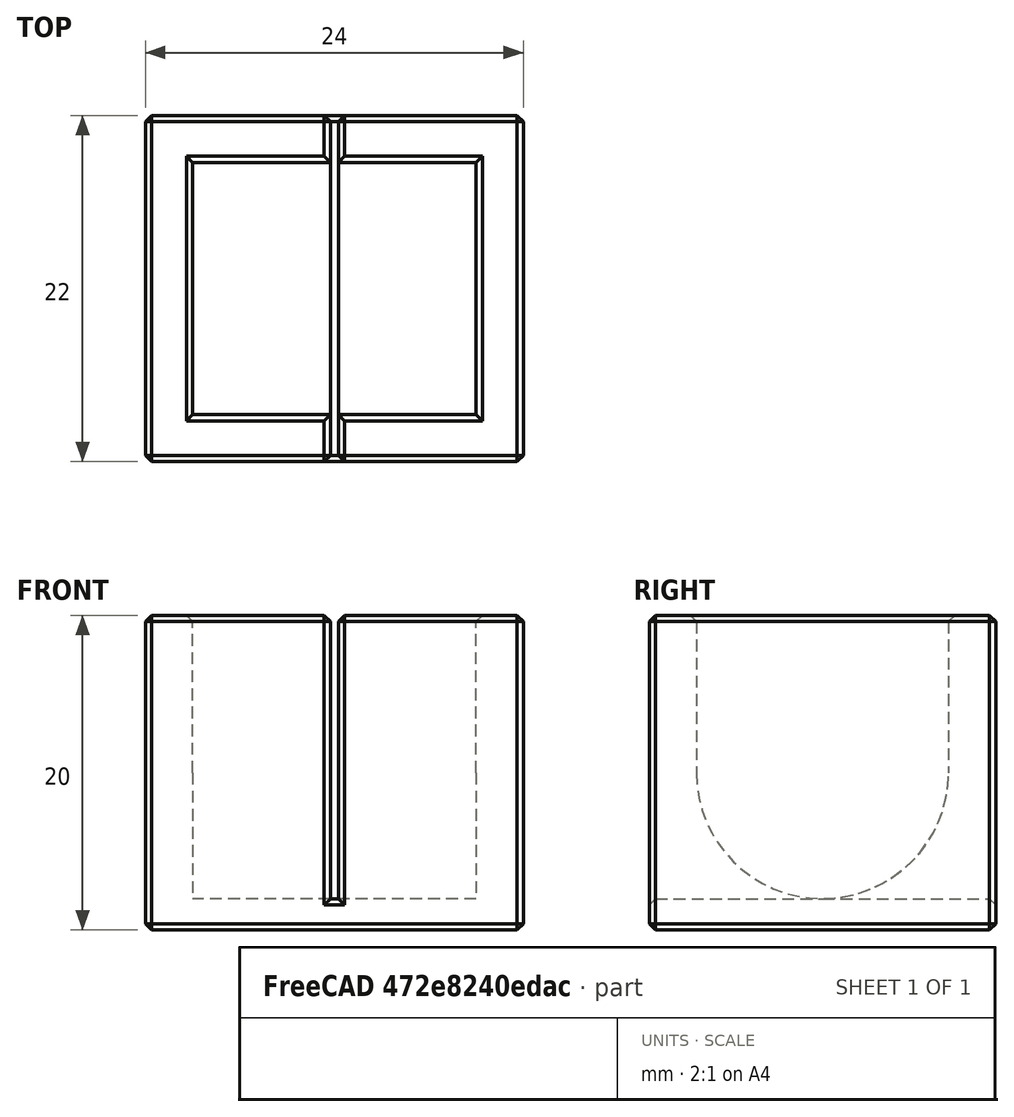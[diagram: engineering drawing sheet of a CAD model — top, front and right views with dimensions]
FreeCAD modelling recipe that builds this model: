
FCSTD DOCUMENT  (FreeCAD 0.19R24291 (Git))
Label: silicon-spacer-cut-template
License: Other
LicenseURL: GPL3
objects: Part::Box×3, Part::Cut×2, Part::Cylinder×1, Part::MultiFuse×1, Part::Chamfer×1
note: 8 computed .brp shape members not serialized (recipe doc carries the construction recipe); baked Part::Feature solids carry a one-line shape summary decoded from their .brp

FEATURE [Part::Cylinder] Cylinder
  Angle = 360
  AttacherType = Attacher::AttachEngine3D
  Height = 18
  Placement = pos=(8,0,10) rot=(0,1,0;4.71239rad)
  Radius = 8
FEATURE [Part::Box] Box  label="Cube"
  AttacherType = Attacher::AttachEngine3D
  Height = 20
  Length = 24
  Placement = pos=(-13,-11,0) rot=(0,0,1;0rad)
  Width = 22
FEATURE [Part::Box] Box001  label="Cube001"
  AttacherType = Attacher::AttachEngine3D
  Height = 10
  Length = 18
  Placement = pos=(-10,-8,10) rot=(0,0,1;0rad)
  Width = 16
FEATURE [Part::MultiFuse] Fusion
  Shapes = -> [Box001,Cylinder]
FEATURE [Part::Cut] Cut
  Base = -> Box
  Tool = -> Fusion
FEATURE [Part::Box] Box002  label="Cube002"
  AttacherType = Attacher::AttachEngine3D
  Height = 24
  Length = 0.5
  Placement = pos=(-1.25,-13,2) rot=(0,0,1;0rad)
  Width = 26
FEATURE [Part::Cut] Cut001
  Base = -> Cut
  Tool = -> Box002
FEATURE [Part::Chamfer] Chamfer
  Base = -> Cut001
  Edges = 30 edges r=0.4: [Edge1,Edge2,Edge3,Edge4,Edge5,Edge6,Edge7,Edge8,Edge9,Edge10,Edge11,Edge12,Edge13,Edge14,Edge15,Edge16,Edge17,Edge18,Edge19,Edge20,Edge21,Edge22,Edge23,Edge24,Edge25,Edge26,Edge27,Edge28,Edge29,Edge30]
